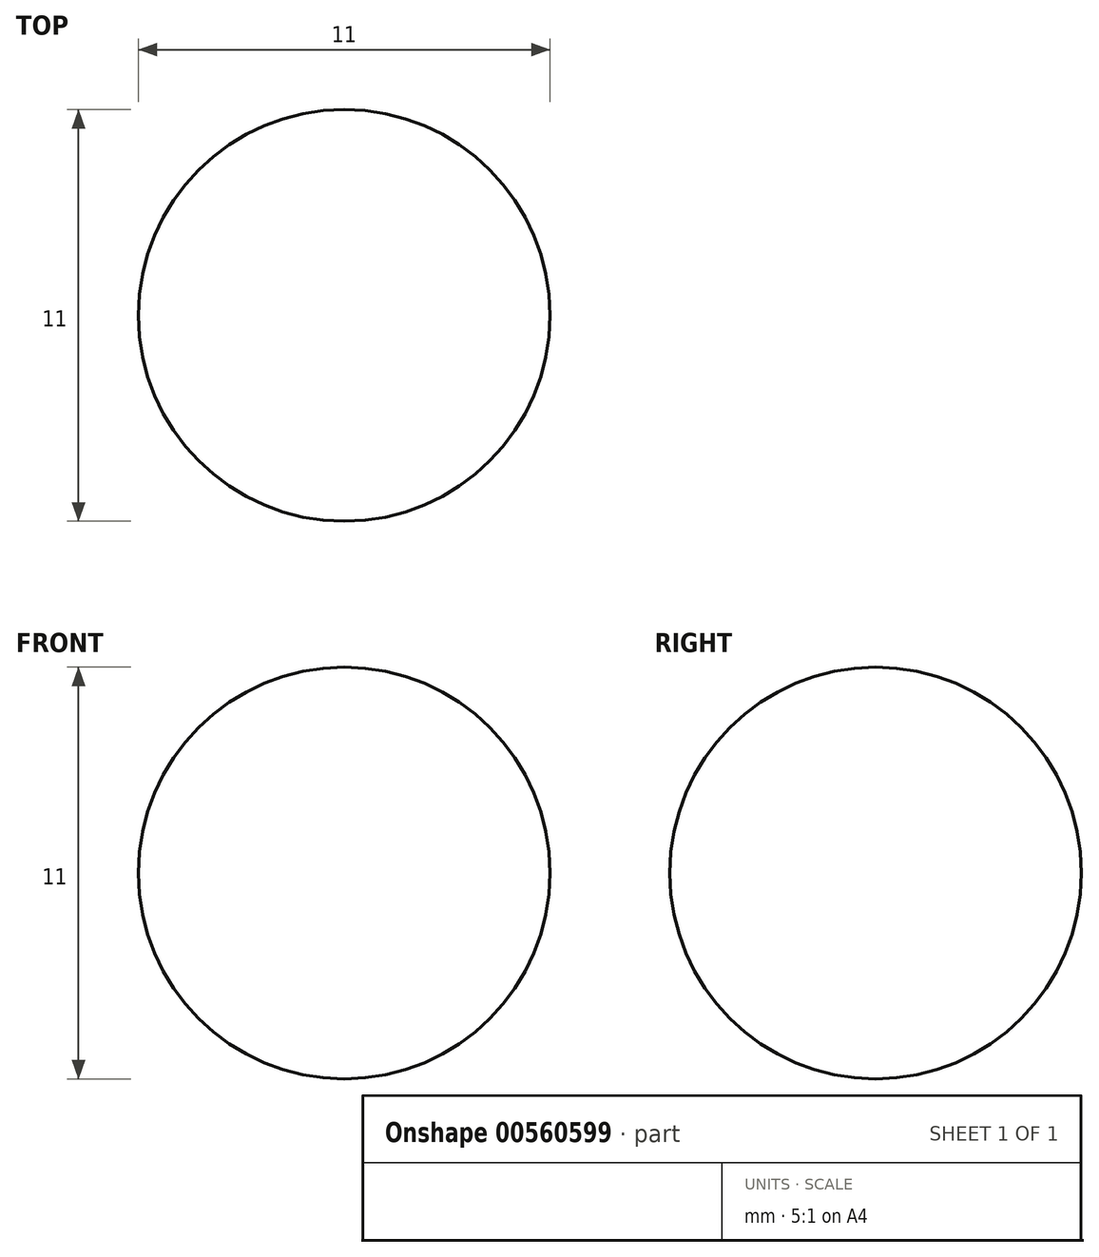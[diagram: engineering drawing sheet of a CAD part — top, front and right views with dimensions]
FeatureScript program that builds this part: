
annotation { "Feature Type Name" : "Feature", "Feature Type Description" : "" }
export const myFeature = defineFeature(function(context is Context, id is Id, definition is map)
    precondition{}
    {
        {
            var Q0;
            Q0=qCreatedBy(makeId("Right.planeOp"),FACE);
            var sketch = newSketch(context, id + "F0", { "sketchPlane" : qUnion([Q0])});
            skArc(sketch, "E0", {"start": v(0, -5.5) * mm, "mid": v(5.5, 0) * mm, "end": v(0, 5.5) * mm});
            skLineSegment(sketch, "E1", {"start": v(0, 0) * mm, "end": v(0, 5.5) * mm});
            skLineSegment(sketch, "E2", {"start": v(0, 0) * mm, "end": v(0, -5.5) * mm});
            skSolve(sketch);
        }
        {
            var Q0;
            Q0=makeQuery(id+"F0.imprint","IMPRINT",FACE,{"disambiguationData":[TD([[makeQuery(id+"F0.imprint","IMPRINT",EDGE,{"derivedFrom":sQuery(id+"F0.wireOp",EDGE,"E0")}),1.0]])]});
            var Q1;
            Q1=sQuery(id+"F0.wireOp",EDGE,"E1");
            revolve(context, id + "F1", {"entities" : qUnion([Q0]), "axis" : qUnion([Q1]), "revolveType" : RevolveType.FULL});
        }
    });
